# Revit family: MTCV_DN15-20_RFA_1
name_source: partatom
category: Pipe Accessories
units: mm (PartAtom-declared; Revit-internal decimal feet)

## family parameters
Always vertical = Yes
Cut with Voids When Loaded = No
OmniClass Number = 23.75.65.14.14.17
OmniClass Title = Flow Controls
Part Type = Valve - Breaks Into
Round Connector Dimension = Use Diameter
Shared = No
Work Plane-Based = No

## types (14) — shared parameters
Connection = Internal thread
Description = Thermostatic Balancing Valve
IfcExportAs = IfcValveType
IfcExportType = MTCV
L2 = 15 mm  [stored 0.0492126 ft]
L5 = 3 mm  [stored 0.00984252 ft]
L6 = 4 mm  [stored 0.0131234 ft]
L7 = 8 mm  [stored 0.0262467 ft]
LOD 200 = No
LOD 350 = Yes
Manufacturer = Danfoss
Max Medium Temperature = 100 °C
Max Temperature Setting = 60 °C
Min Temperature Setting = 35 °C
Nominal Pressure = PN 10
URL = https://store.danfoss.com

## per-type parameters (varying)
| type | D | D3 | D4 | D5 | D6 | D7 | D8 | Kvs | L | L1 | L10 | L3 | L4 | L8 | L9 | Model | Model Type | Valve Body Material | Version | Weight |
| MTCV 0_DN15_003Z0514 | 15 mm  [stored 0.0492126 ft] | 27 mm  [stored 0.0885827 ft] | 26 mm  [stored 0.0853018 ft] | 22 mm  [stored 0.0721785 ft] | 19 mm  [stored 0.062336 ft] | 26 mm  [stored 0.0853018 ft] | 29 mm  [stored 0.0951444 ft] | 1.5 m³/h | 75 mm | 30 mm  [stored 0.0984252 ft] | 3 mm  [stored 0.00984252 ft] | 10 mm  [stored 0.0328084 ft] | 7 mm  [stored 0.0229659 ft] | 3 mm  [stored 0.00984252 ft] | 10 mm  [stored 0.0328084 ft] | 003Z0514 | MTCV 0_DN15 | Danfoss Bronze (Rg5) | 0 | 0.56 kg |
| MTCV 0_DN20_003Z0553 | 20 mm  [stored 0.0656168 ft] | 32 mm  [stored 0.104987 ft] | 30 mm  [stored 0.0984252 ft] | 28 mm  [stored 0.0918635 ft] | 26 mm  [stored 0.0853018 ft] | 30 mm  [stored 0.0984252 ft] | 36 mm | 1.8 m³/h | 80 mm  [stored 0.262467 ft] | 33 mm  [stored 0.108268 ft] | 6 mm  [stored 0.019685 ft] | 14 mm  [stored 0.0459318 ft] | 4 mm  [stored 0.0131234 ft] | 4 mm  [stored 0.0131234 ft] | 14 mm  [stored 0.0459318 ft] | 003Z0553 | MTCV 0_DN20 | Danfoss Bronze (Rg5) | 0 | 0.62 kg |
| MTCV A_DN15_003Z4515 | 15 mm  [stored 0.0492126 ft] | 27 mm  [stored 0.0885827 ft] | 26 mm  [stored 0.0853018 ft] | 22 mm  [stored 0.0721785 ft] | 19 mm  [stored 0.062336 ft] | 26 mm  [stored 0.0853018 ft] | 29 mm  [stored 0.0951444 ft] | 1.5 m³/h | 75 mm | 30 mm  [stored 0.0984252 ft] | 3 mm  [stored 0.00984252 ft] | 10 mm  [stored 0.0328084 ft] | 7 mm  [stored 0.0229659 ft] | 3 mm  [stored 0.00984252 ft] | 10 mm  [stored 0.0328084 ft] | 003Z4515, 003Z0535 | MTCV A_DN15 | Danfoss Bronze (Rg5) | A | 0.56 kg |
| MTCV A_DN20_003Z4520 | 20 mm  [stored 0.0656168 ft] | 32 mm  [stored 0.104987 ft] | 30 mm  [stored 0.0984252 ft] | 28 mm  [stored 0.0918635 ft] | 26 mm  [stored 0.0853018 ft] | 30 mm  [stored 0.0984252 ft] | 36 mm | 1.8 m³/h | 80 mm  [stored 0.262467 ft] | 33 mm  [stored 0.108268 ft] | 6 mm  [stored 0.019685 ft] | 14 mm  [stored 0.0459318 ft] | 4 mm  [stored 0.0131234 ft] | 4 mm  [stored 0.0131234 ft] | 14 mm  [stored 0.0459318 ft] | 003Z4520, 003Z0540 | MTCV A_DN20 | Danfoss Bronze (Rg5) | A | 0.62 kg |
| MTCV B_DN15_003Z1511 | 15 mm  [stored 0.0492126 ft] | 27 mm  [stored 0.0885827 ft] | 26 mm  [stored 0.0853018 ft] | 22 mm  [stored 0.0721785 ft] | 19 mm  [stored 0.062336 ft] | 26 mm  [stored 0.0853018 ft] | 29 mm  [stored 0.0951444 ft] | 1.5 m³/h | 75 mm | 30 mm  [stored 0.0984252 ft] | 3 mm  [stored 0.00984252 ft] | 10 mm  [stored 0.0328084 ft] | 7 mm  [stored 0.0229659 ft] | 3 mm  [stored 0.00984252 ft] | 10 mm  [stored 0.0328084 ft] | 003Z1511 | MTCV B_DN15 | Danfoss Bronze (Rg5) | B | 0.56 kg |
| MTCV B_DN20_003Z1557 | 20 mm  [stored 0.0656168 ft] | 32 mm  [stored 0.104987 ft] | 30 mm  [stored 0.0984252 ft] | 28 mm  [stored 0.0918635 ft] | 26 mm  [stored 0.0853018 ft] | 30 mm  [stored 0.0984252 ft] | 36 mm | 1.8 m³/h | 80 mm  [stored 0.262467 ft] | 33 mm  [stored 0.108268 ft] | 6 mm  [stored 0.019685 ft] | 14 mm  [stored 0.0459318 ft] | 4 mm  [stored 0.0131234 ft] | 4 mm  [stored 0.0131234 ft] | 14 mm  [stored 0.0459318 ft] | 003Z1557 | MTCV B_DN20 | Danfoss Bronze (Rg5) | B | 0.62 kg |
| MTCV C_DN15 | 15 mm  [stored 0.0492126 ft] | 27 mm  [stored 0.0885827 ft] | 26 mm  [stored 0.0853018 ft] | 22 mm  [stored 0.0721785 ft] | 19 mm  [stored 0.062336 ft] | 26 mm  [stored 0.0853018 ft] | 29 mm  [stored 0.0951444 ft] | 1.5 m³/h | 75 mm | 30 mm  [stored 0.0984252 ft] | 3 mm  [stored 0.00984252 ft] | 10 mm  [stored 0.0328084 ft] | 7 mm  [stored 0.0229659 ft] | 3 mm  [stored 0.00984252 ft] | 10 mm  [stored 0.0328084 ft] |  | MTCV C_DN15 | Danfoss Bronze (Rg5) | C | 0.56 kg |
| MTCV C_DN20 | 20 mm  [stored 0.0656168 ft] | 32 mm  [stored 0.104987 ft] | 30 mm  [stored 0.0984252 ft] | 28 mm  [stored 0.0918635 ft] | 26 mm  [stored 0.0853018 ft] | 30 mm  [stored 0.0984252 ft] | 36 mm | 1.8 m³/h | 80 mm  [stored 0.262467 ft] | 33 mm  [stored 0.108268 ft] | 6 mm  [stored 0.019685 ft] | 14 mm  [stored 0.0459318 ft] | 4 mm  [stored 0.0131234 ft] | 4 mm  [stored 0.0131234 ft] | 14 mm  [stored 0.0459318 ft] |  | MTCV C_DN20 | Danfoss Bronze (Rg5) | C | 0.62 kg |
| MTCV DVGW_DN15_003Z0510 | 15 mm  [stored 0.0492126 ft] | 27 mm  [stored 0.0885827 ft] | 26 mm  [stored 0.0853018 ft] | 22 mm  [stored 0.0721785 ft] | 19 mm  [stored 0.062336 ft] | 26 mm  [stored 0.0853018 ft] | 29 mm  [stored 0.0951444 ft] | 1.5 m³/h | 75 mm | 30 mm  [stored 0.0984252 ft] | 3 mm  [stored 0.00984252 ft] | 10 mm  [stored 0.0328084 ft] | 7 mm  [stored 0.0229659 ft] | 3 mm  [stored 0.00984252 ft] | 10 mm  [stored 0.0328084 ft] | 003Z0510 | MTCV DVGW_DN15 | Danfoss Bronze (Rg5) | A | 0.56 kg |
| MTCV NL_DN20_003Z0551 | 20 mm  [stored 0.0656168 ft] | 32 mm  [stored 0.104987 ft] | 30 mm  [stored 0.0984252 ft] | 28 mm  [stored 0.0918635 ft] | 26 mm  [stored 0.0853018 ft] | 30 mm  [stored 0.0984252 ft] | 36 mm | 1.8 m³/h | 80 mm  [stored 0.262467 ft] | 33 mm  [stored 0.108268 ft] | 6 mm  [stored 0.019685 ft] | 14 mm  [stored 0.0459318 ft] | 4 mm  [stored 0.0131234 ft] | 4 mm  [stored 0.0131234 ft] | 14 mm  [stored 0.0459318 ft] | 003Z0551 | MTCV NL_DN20 | Danfoss Bronze (Rg5) | A | 0.62 kg |
| MTCV NL_DN15_003Z0516 | 15 mm  [stored 0.0492126 ft] | 27 mm  [stored 0.0885827 ft] | 26 mm  [stored 0.0853018 ft] | 22 mm  [stored 0.0721785 ft] | 19 mm  [stored 0.062336 ft] | 26 mm  [stored 0.0853018 ft] | 29 mm  [stored 0.0951444 ft] | 1.5 m³/h | 75 mm | 30 mm  [stored 0.0984252 ft] | 3 mm  [stored 0.00984252 ft] | 10 mm  [stored 0.0328084 ft] | 7 mm  [stored 0.0229659 ft] | 3 mm  [stored 0.00984252 ft] | 10 mm  [stored 0.0328084 ft] | 003Z0516 | MTCV NL_DN15 | Danfoss Bronze (Rg5) | A | 0.56 kg |
| MTCV DVGW_DN20_003Z0558 | 20 mm  [stored 0.0656168 ft] | 32 mm  [stored 0.104987 ft] | 30 mm  [stored 0.0984252 ft] | 28 mm  [stored 0.0918635 ft] | 26 mm  [stored 0.0853018 ft] | 30 mm  [stored 0.0984252 ft] | 36 mm | 1.8 m³/h | 80 mm  [stored 0.262467 ft] | 33 mm  [stored 0.108268 ft] | 6 mm  [stored 0.019685 ft] | 14 mm  [stored 0.0459318 ft] | 4 mm  [stored 0.0131234 ft] | 4 mm  [stored 0.0131234 ft] | 14 mm  [stored 0.0459318 ft] | 003Z0558 | MTCV DVGW_DN20 | Danfoss Bronze (Rg5) | A | 0.62 kg |
| MTCV A PURE_DN15_003Z6515 | 15 mm  [stored 0.0492126 ft] | 27 mm  [stored 0.0885827 ft] | 26 mm  [stored 0.0853018 ft] | 22 mm  [stored 0.0721785 ft] | 19 mm  [stored 0.062336 ft] | 26 mm  [stored 0.0853018 ft] | 29 mm  [stored 0.0951444 ft] | 1.5 m³/h | 75 mm | 30 mm  [stored 0.0984252 ft] | 3 mm  [stored 0.00984252 ft] | 10 mm  [stored 0.0328084 ft] | 7 mm  [stored 0.0229659 ft] | 3 mm  [stored 0.00984252 ft] | 10 mm  [stored 0.0328084 ft] | 003Z6515 | MTCV A PURE_DN15 | Danfoss Bronze (Lead Free Rg+) | A | 0.56 kg |
| MTCV A PURE_DN20_003Z6520 | 20 mm  [stored 0.0656168 ft] | 32 mm  [stored 0.104987 ft] | 30 mm  [stored 0.0984252 ft] | 28 mm  [stored 0.0918635 ft] | 26 mm  [stored 0.0853018 ft] | 30 mm  [stored 0.0984252 ft] | 36 mm | 1.8 m³/h | 80 mm  [stored 0.262467 ft] | 33 mm  [stored 0.108268 ft] | 6 mm  [stored 0.019685 ft] | 14 mm  [stored 0.0459318 ft] | 4 mm  [stored 0.0131234 ft] | 4 mm  [stored 0.0131234 ft] | 14 mm  [stored 0.0459318 ft] | 003Z6520 | MTCV A PURE_DN20 | Danfoss Bronze (Lead Free Rg+) | A | 0.62 kg |

note: [stored X ft] marks values corroborated as IEEE doubles in the binary element streams (Revit-internal decimal feet)

## geometry (parser evidence)
native form markers: Sweep x17
no freeform markers — native parametric forms only
